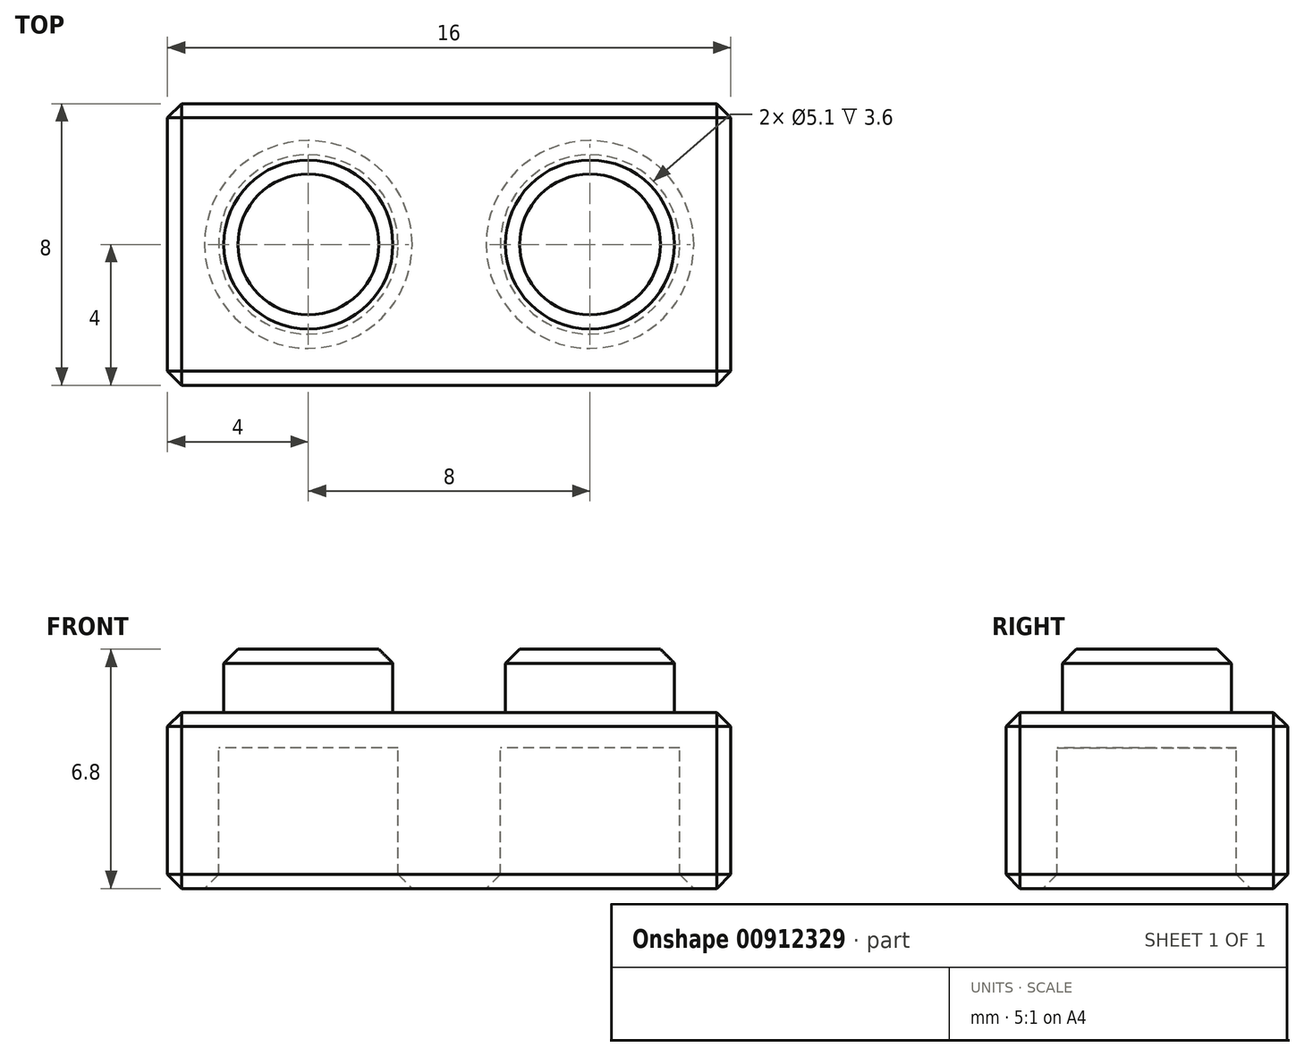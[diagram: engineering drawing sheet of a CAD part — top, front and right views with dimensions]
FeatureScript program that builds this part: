
annotation { "Feature Type Name" : "Feature", "Feature Type Description" : "" }
export const myFeature = defineFeature(function(context is Context, id is Id, definition is map)
    precondition{}
    {
        {
            var Q0;
            Q0=qCreatedBy(makeId("Top.planeOp"),FACE);
            var sketch = newSketch(context, id + "F0", { "sketchPlane" : qUnion([Q0])});
            skLineSegment(sketch, "E0.bottom", {"start": v(-8, 4) * mm, "end": v(8, 4) * mm});
            skLineSegment(sketch, "E0.top", {"start": v(-8, -4) * mm, "end": v(8, -4) * mm});
            skLineSegment(sketch, "E0.left", {"start": v(-8, 4) * mm, "end": v(-8, -4) * mm});
            skLineSegment(sketch, "E0.right", {"start": v(8, 4) * mm, "end": v(8, -4) * mm});
            skCircle(sketch, "E1", {"center": v(-4, 0) * mm, "radius": 2.55 * mm});
            skCircle(sketch, "E2", {"center": v(-4, 0) * mm, "radius": 2.4 * mm});
            skCircle(sketch, "E3", {"center": v(-4, 0) * mm, "radius": 3 * mm});
            skCircle(sketch, "E4.1.0.0", {"center": v(4, 0) * mm, "radius": 3 * mm});
            skCircle(sketch, "E4.1.0.1", {"center": v(4, 0) * mm, "radius": 2.55 * mm});
            skCircle(sketch, "E4.1.0.2", {"center": v(4, 0) * mm, "radius": 2.4 * mm});
            skLineSegment(sketch, "E4.direction1", {"start": v(-4, 0) * mm, "end": v(4, 0) * mm, "construction": true});
            skLineSegment(sketch, "E5.0", {"start": v(-7, 3) * mm, "end": v(7, 3) * mm});
            skLineSegment(sketch, "E5.1", {"start": v(-7, 3) * mm, "end": v(-7, -3) * mm});
            skLineSegment(sketch, "E6.0", {"start": v(-7, -3) * mm, "end": v(7, -3) * mm});
            skLineSegment(sketch, "E6.1", {"start": v(7, 3) * mm, "end": v(7, -3) * mm});
            skSolve(sketch);
        }
        {
            var Q0;
            Q0=qSketchRegion(id+"F0",true);
            var Q1;
            Q1=makeQuery(id+"F0.imprint","IMPRINT",FACE,{"disambiguationData":[TD([[makeQuery(id+"F0.imprint","IMPRINT",EDGE,{"derivedFrom":sQuery(id+"F0.wireOp",EDGE,"E3")}),-1.0]])]});
            var Q2;
            Q2=makeQuery(id+"F0.imprint","IMPRINT",FACE,{"disambiguationData":[TD([[makeQuery(id+"F0.imprint","IMPRINT",EDGE,{"derivedFrom":sQuery(id+"F0.wireOp",EDGE,"E1")}),1.0]])]});
            var Q3;
            Q3=makeQuery(id+"F0.imprint","IMPRINT",FACE,{"disambiguationData":[TD([[makeQuery(id+"F0.imprint","IMPRINT",EDGE,{"derivedFrom":sQuery(id+"F0.wireOp",EDGE,"E1")}),-1.0]])]});
            var Q4;
            Q4=makeQuery(id+"F0.imprint","IMPRINT",FACE,{"disambiguationData":[TD([[makeQuery(id+"F0.imprint","IMPRINT",EDGE,{"derivedFrom":sQuery(id+"F0.wireOp",EDGE,"E4.1.0.1")}),1.0]])]});
            var Q5;
            Q5=makeQuery(id+"F0.imprint","IMPRINT",FACE,{"disambiguationData":[TD([[makeQuery(id+"F0.imprint","IMPRINT",EDGE,{"derivedFrom":sQuery(id+"F0.wireOp",EDGE,"E4.1.0.0")}),1.0]])]});
            var Q6;
            Q6=makeQuery(id+"F0.imprint","IMPRINT",FACE,{"disambiguationData":[TD([[makeQuery(id+"F0.imprint","IMPRINT",EDGE,{"derivedFrom":sQuery(id+"F0.wireOp",EDGE,"E4.1.0.2")}),1.0]])]});
            var Q7;
            Q7=makeQuery(id+"F0.imprint","IMPRINT",FACE,{"disambiguationData":[TD([[makeQuery(id+"F0.imprint","IMPRINT",EDGE,{"derivedFrom":sQuery(id+"F0.wireOp",EDGE,"E2")}),1.0]])]});
            var Q8;
            Q8=makeQuery(id+"F0.imprint","IMPRINT",FACE,{"disambiguationData":[TD([[makeQuery(id+"F0.imprint","IMPRINT",EDGE,{"derivedFrom":sQuery(id+"F0.wireOp",EDGE,"E5.0")}),-1.0]])]});
            var Q9;
            {var subQ0=sQuery(id+"F0.wireOp",EDGE,"3dca042f-c229-4d8a-b28b-e1ef92b8f3bf.trimOffspring");Q9=makeQuery(id+"F0.imprint","IMPRINT",FACE,{"disambiguationData":[TD([[makeQuery(id+"F0.imprint","IMPRINT",EDGE,{"derivedFrom":subQ0}),1.0]])]});}
            var Q10;
            {var subQ0=sQuery(id+"F0.wireOp",EDGE,"3f71be82-b088-41be-a58b-1d14fe589e35.trimOffspring");Q10=makeQuery(id+"F0.imprint","IMPRINT",FACE,{"disambiguationData":[TD([[makeQuery(id+"F0.imprint","IMPRINT",EDGE,{"derivedFrom":subQ0}),-1.0]])]});}
            var Q11;
            {var subQ0=sQuery(id+"F0.wireOp",EDGE,"E6.1");var subQ1=sQuery(id+"F0.wireOp",EDGE,"E4.1.0.0");var subQ2=makeQuery(id+"F0.imprint","INTERSECT",VERTEX,{"derivedFrom":[subQ1,subQ0]});Q11=makeQuery(id+"F0.imprint","IMPRINT",FACE,{"disambiguationData":[TD([[makeQuery(id+"F0.imprint","IMPRINT",EDGE,{"disambiguationData":[TD([[subQ2,1.0]])],"derivedFrom":subQ1}),-1.0]])]});}
            var Q12;
            {var subQ0=sQuery(id+"F0.wireOp",EDGE,"3dca042f-c229-4d8a-b28b-e1ef92b8f3bf.trimOffspring");Q12=makeQuery(id+"F0.imprint","IMPRINT",FACE,{"disambiguationData":[TD([[makeQuery(id+"F0.imprint","IMPRINT",EDGE,{"derivedFrom":subQ0}),-1.0]])]});}
            extrude(context, id + "F1", {"entities" : qUnion([Q0, Q1, Q2, Q3, Q4, Q5, Q6, Q7, Q8, Q9, Q10, Q11, Q12]), "oppositeDirection" : true, "depth" : 1 * mm, "offsetDistance" : 25 * mm});
        }
        {
            var Q0;
            Q0=makeQuery(id+"F0.imprint","IMPRINT",FACE,{"disambiguationData":[TD([[makeQuery(id+"F0.imprint","IMPRINT",EDGE,{"derivedFrom":sQuery(id+"F0.wireOp",EDGE,"E2")}),1.0]])]});
            var Q1;
            Q1=makeQuery(id+"F0.imprint","IMPRINT",FACE,{"disambiguationData":[TD([[makeQuery(id+"F0.imprint","IMPRINT",EDGE,{"derivedFrom":sQuery(id+"F0.wireOp",EDGE,"E4.1.0.2")}),1.0]])]});
            extrude(context, id + "F2", {"entities" : qUnion([Q0, Q1]), "operationType" : NewBodyOperationType.ADD, "depth" : 1.8 * mm, "offsetDistance" : 25 * mm});
        }
        {
            var Q0;
            Q0=makeQuery(id+"F0.imprint","IMPRINT",FACE,{"disambiguationData":[TD([[makeQuery(id+"F0.imprint","IMPRINT",EDGE,{"derivedFrom":sQuery(id+"F0.wireOp",EDGE,"E4.1.0.0")}),1.0]])]});
            var Q1;
            Q1=makeQuery(id+"F0.imprint","IMPRINT",FACE,{"disambiguationData":[TD([[makeQuery(id+"F0.imprint","IMPRINT",EDGE,{"derivedFrom":sQuery(id+"F0.wireOp",EDGE,"E3")}),-1.0]])]});
            var Q2;
            Q2=makeQuery(id+"F0.imprint","IMPRINT",FACE,{"disambiguationData":[TD([[makeQuery(id+"F0.imprint","IMPRINT",EDGE,{"derivedFrom":sQuery(id+"F0.wireOp",EDGE,"E0.bottom")}),-1.0]])]});
            var Q3;
            Q3=makeQuery(id+"F0.imprint","IMPRINT",FACE,{"disambiguationData":[TD([[makeQuery(id+"F0.imprint","IMPRINT",EDGE,{"derivedFrom":sQuery(id+"F0.wireOp",EDGE,"E1")}),-1.0]])]});
            extrude(context, id + "F3", {"entities" : qUnion([Q0, Q1, Q2, Q3]), "operationType" : NewBodyOperationType.ADD, "oppositeDirection" : true, "depth" : 5 * mm, "offsetDistance" : 25 * mm});
        }
        {
            var Q0;
            Q0=makeQuery(id+"F2.opExtrude","CAP_FACE",FACE,{"disambiguationData":[OSD([sQuery(id+"F0.wireOp",EDGE,"E2")])],"isStart":false});
            var Q1;
            Q1=makeQuery(id+"F2.opExtrude","CAP_FACE",FACE,{"disambiguationData":[OSD([sQuery(id+"F0.wireOp",EDGE,"E4.1.0.2")])],"isStart":false});
            var Q2;
            {var subQ0=sQuery(id+"F0.wireOp",EDGE,"E0.top");Q2=makeQuery(id+"F3.boolean.opBoolean","MERGE",FACE,{"derivedFrom":[makeQuery(id+"F1.opExtrude","SWEPT_FACE",FACE,{"disambiguationData":[OSD([subQ0])]}),makeQuery(id+"F3.opExtrude","SWEPT_FACE",FACE,{"disambiguationData":[OSD([subQ0])]})]});}
            var Q3;
            {var subQ0=sQuery(id+"F0.wireOp",EDGE,"E0.left");Q3=makeQuery(id+"F3.boolean.opBoolean","MERGE",FACE,{"derivedFrom":[makeQuery(id+"F1.opExtrude","SWEPT_FACE",FACE,{"disambiguationData":[OSD([subQ0])]}),makeQuery(id+"F3.opExtrude","SWEPT_FACE",FACE,{"disambiguationData":[OSD([subQ0])]})]});}
            var Q4;
            {var subQ0=sQuery(id+"F0.wireOp",EDGE,"E0.bottom");Q4=makeQuery(id+"F3.boolean.opBoolean","MERGE",FACE,{"derivedFrom":[makeQuery(id+"F1.opExtrude","SWEPT_FACE",FACE,{"disambiguationData":[OSD([subQ0])]}),makeQuery(id+"F3.opExtrude","SWEPT_FACE",FACE,{"disambiguationData":[OSD([subQ0])]})]});}
            var Q5;
            {var subQ0=sQuery(id+"F0.wireOp",EDGE,"E0.right");Q5=makeQuery(id+"F3.boolean.opBoolean","MERGE",FACE,{"derivedFrom":[makeQuery(id+"F1.opExtrude","SWEPT_FACE",FACE,{"disambiguationData":[OSD([subQ0])]}),makeQuery(id+"F3.opExtrude","SWEPT_FACE",FACE,{"disambiguationData":[OSD([subQ0])]})]});}
            var Q6;
            Q6=makeQuery(id+"F3.opExtrude","CAP_FACE",FACE,{"disambiguationData":[OSD([sQuery(id+"F0.wireOp",EDGE,"E0.bottom"),sQuery(id+"F0.wireOp",EDGE,"E0.top"),sQuery(id+"F0.wireOp",EDGE,"E0.left"),sQuery(id+"F0.wireOp",EDGE,"E0.right"),sQuery(id+"F0.wireOp",EDGE,"E1"),sQuery(id+"F0.wireOp",EDGE,"E4.1.0.1")])],"isStart":false});
            chamfer(context, id + "F4", {"entities" : qUnion([Q0, Q1, Q2, Q3, Q4, Q5, Q6]), "width" : .4 * mm, "tangentPropagation" : true});
        }
    });
